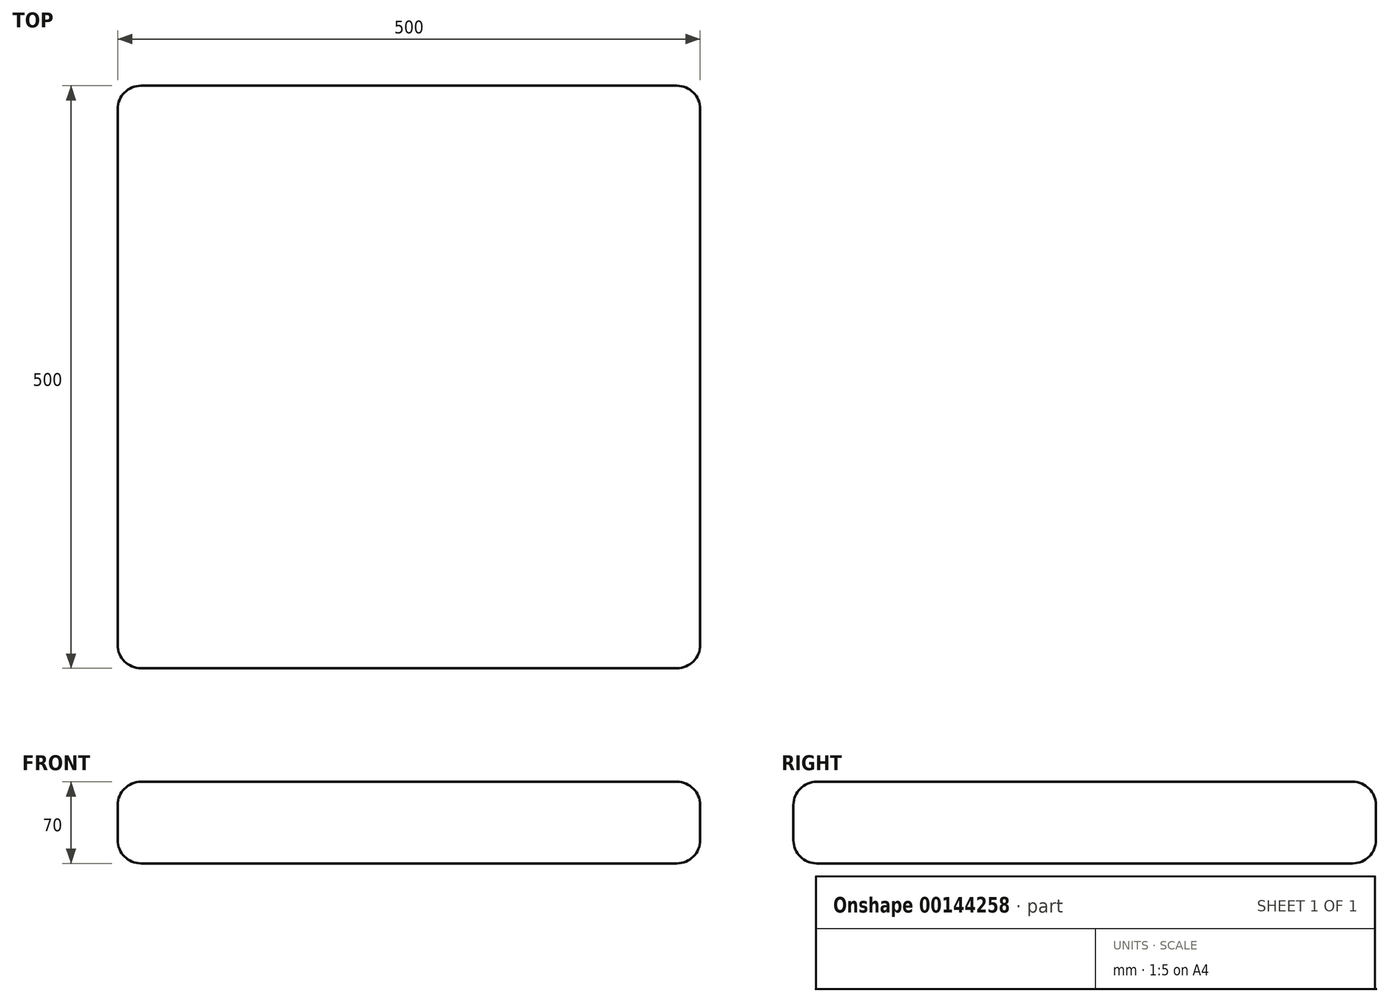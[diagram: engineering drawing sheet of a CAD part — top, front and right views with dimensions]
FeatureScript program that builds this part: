
annotation { "Feature Type Name" : "Feature", "Feature Type Description" : "" }
export const myFeature = defineFeature(function(context is Context, id is Id, definition is map)
    precondition{}
    {
        {
            var Q0;
            Q0=qCreatedBy(makeId("Top.planeOp"),FACE);
            var sketch = newSketch(context, id + "F0", { "sketchPlane" : qUnion([Q0])});
            skLineSegment(sketch, "E0.bottom", {"start": v(0, 0) * mm, "end": v(500, 0) * mm});
            skLineSegment(sketch, "E0.top", {"start": v(0, 500) * mm, "end": v(500, 500) * mm});
            skLineSegment(sketch, "E0.left", {"start": v(0, 0) * mm, "end": v(0, 500) * mm});
            skLineSegment(sketch, "E0.right", {"start": v(500, 0) * mm, "end": v(500, 500) * mm});
            skSolve(sketch);
        }
        {
            var Q0;
            Q0 = qSketchRegion(id + "F0", true);
            extrude(context, id + "F1", {"entities" : qUnion([Q0]), "depth" : 70 * mm});
        }
        {
            var Q0;
            Q0=makeQuery(id+"F1.opExtrude","SWEPT_EDGE",EDGE,{"disambiguationData":[OSD([sQuery(id+"F0.wireOp",EDGE,"E0.bottom"),sQuery(id+"F0.wireOp",EDGE,"E0.right")])]});
            var Q1;
            Q1=makeQuery(id+"F1.opExtrude","SWEPT_EDGE",EDGE,{"disambiguationData":[OSD([sQuery(id+"F0.wireOp",EDGE,"E0.top"),sQuery(id+"F0.wireOp",EDGE,"E0.left")])]});
            var Q2;
            Q2=makeQuery(id+"F1.opExtrude","SWEPT_EDGE",EDGE,{"disambiguationData":[OSD([sQuery(id+"F0.wireOp",EDGE,"E0.top"),sQuery(id+"F0.wireOp",EDGE,"E0.right")])]});
            var Q3;
            Q3=makeQuery(id+"F1.opExtrude","CAP_EDGE",EDGE,{"disambiguationData":[OSD([sQuery(id+"F0.wireOp",EDGE,"E0.bottom")])],"isStart":false});
            var Q4;
            Q4=makeQuery(id+"F1.opExtrude","CAP_EDGE",EDGE,{"disambiguationData":[OSD([sQuery(id+"F0.wireOp",EDGE,"E0.top")])],"isStart":true});
            var Q5;
            Q5=makeQuery(id+"F1.opExtrude","CAP_EDGE",EDGE,{"disambiguationData":[OSD([sQuery(id+"F0.wireOp",EDGE,"E0.top")])],"isStart":false});
            var Q6;
            Q6=makeQuery(id+"F1.opExtrude","CAP_EDGE",EDGE,{"disambiguationData":[OSD([sQuery(id+"F0.wireOp",EDGE,"E0.left")])],"isStart":false});
            var Q7;
            Q7=makeQuery(id+"F1.opExtrude","CAP_EDGE",EDGE,{"disambiguationData":[OSD([sQuery(id+"F0.wireOp",EDGE,"E0.right")])],"isStart":true});
            var Q8;
            Q8=makeQuery(id+"F1.opExtrude","CAP_EDGE",EDGE,{"disambiguationData":[OSD([sQuery(id+"F0.wireOp",EDGE,"E0.right")])],"isStart":false});
            var Q9;
            Q9=makeQuery(id+"F1.opExtrude","SWEPT_EDGE",EDGE,{"disambiguationData":[OSD([sQuery(id+"F0.wireOp",EDGE,"E0.bottom"),sQuery(id+"F0.wireOp",EDGE,"E0.left")])]});
            var Q10;
            Q10=makeQuery(id+"F1.opExtrude","CAP_EDGE",EDGE,{"disambiguationData":[OSD([sQuery(id+"F0.wireOp",EDGE,"E0.bottom")])],"isStart":true});
            var Q11;
            Q11=makeQuery(id+"F1.opExtrude","CAP_EDGE",EDGE,{"disambiguationData":[OSD([sQuery(id+"F0.wireOp",EDGE,"E0.left")])],"isStart":true});
            fillet(context, id + "F2", {"entities" : qUnion([Q0, Q1, Q2, Q3, Q4, Q5, Q6, Q7, Q8, Q9, Q10, Q11]), "radius" : 20 * mm, "tangentPropagation" : true, "allowEdgeOverflow" : false});
        }
    });
